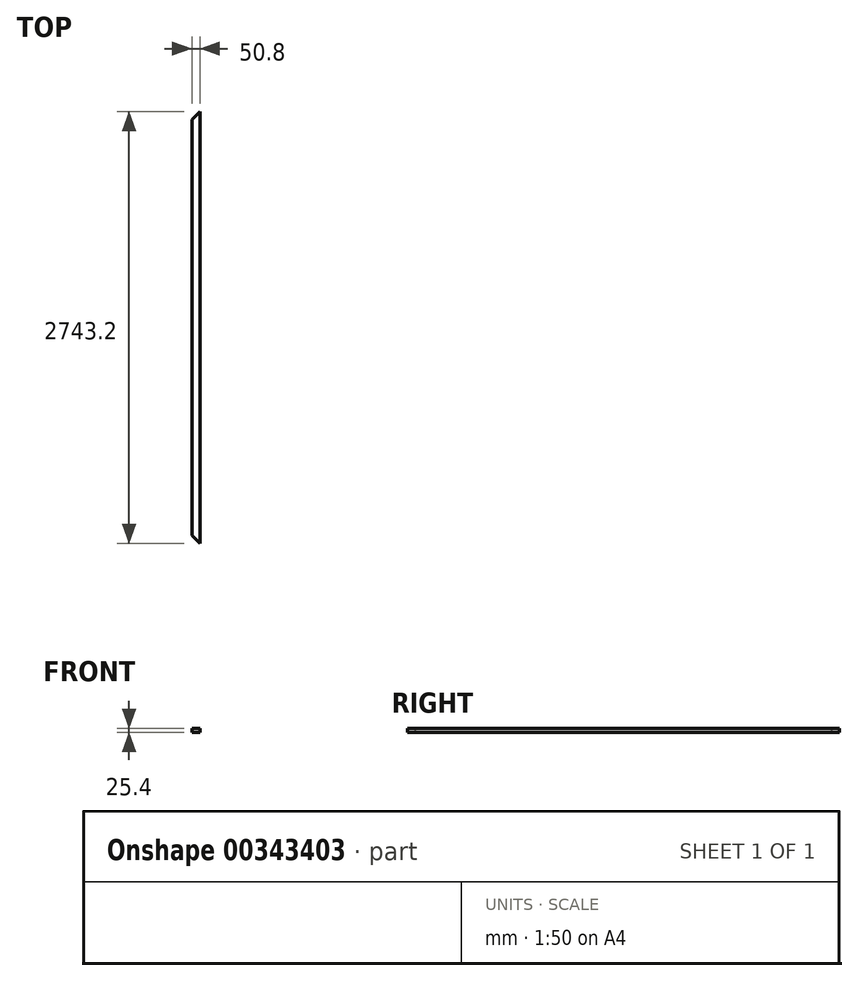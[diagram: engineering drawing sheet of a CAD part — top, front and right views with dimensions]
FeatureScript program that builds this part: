
annotation { "Feature Type Name" : "Feature", "Feature Type Description" : "" }
export const myFeature = defineFeature(function(context is Context, id is Id, definition is map)
    precondition{}
    {
        {
            var Q0;
            Q0=qCreatedBy(makeId("Front.planeOp"),FACE);
            var sketch = newSketch(context, id + "F0", { "sketchPlane" : qUnion([Q0])});
            skLineSegment(sketch, "E0.bottom", {"start": v(-27.4, 24.63) * mm, "end": v(23.4, 24.63) * mm});
            skLineSegment(sketch, "E0.top", {"start": v(-27.4, -0.77) * mm, "end": v(23.4, -0.77) * mm});
            skLineSegment(sketch, "E0.left", {"start": v(-27.4, 24.63) * mm, "end": v(-27.4, -0.77) * mm});
            skLineSegment(sketch, "E0.right", {"start": v(23.4, 24.63) * mm, "end": v(23.4, -0.77) * mm});
            skPoint(sketch, "E0.middle", {"position": v(-2, 11.93) * mm});
            skSolve(sketch);
        }
        {
            var Q0;
            Q0=makeQuery(id+"F0.imprint","IMPRINT",FACE,{"disambiguationData":[TD([[makeQuery(id+"F0.imprint","IMPRINT",EDGE,{"derivedFrom":sQuery(id+"F0.wireOp",EDGE,"E0.bottom")}),-1.0]])]});
            extrude(context, id + "F1", {"entities" : qUnion([Q0]), "depth" : 2743.2 * mm});
        }
        {
            var Q0;
            Q0=makeQuery(id+"F1.opExtrude","CAP_EDGE",EDGE,{"disambiguationData":[OSD([sQuery(id+"F0.wireOp",EDGE,"E0.left")])],"isStart":true});
            chamfer(context, id + "F2", {"entities" : qUnion([Q0]), "width" : 50.8 * mm, "tangentPropagation" : true});
        }
        {
            var Q0;
            Q0=makeQuery(id+"F1.opExtrude","CAP_EDGE",EDGE,{"disambiguationData":[OSD([sQuery(id+"F0.wireOp",EDGE,"E0.left")])],"isStart":false});
            chamfer(context, id + "F3", {"entities" : qUnion([Q0]), "width" : 50.8 * mm, "tangentPropagation" : true});
        }
    });
